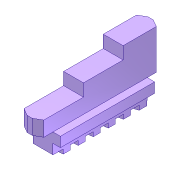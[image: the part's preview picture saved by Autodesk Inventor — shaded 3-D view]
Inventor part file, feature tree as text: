
AUTODESK INVENTOR PART (.ipt)
format: ipt  version: unknown  size: 337,408 bytes
history: native  units: in
note: dims shown in document units (in); Inventor stores cm internally (conversion verified against a paired STEP export)
features: extrude x7, sketch x7, fillet x1, projected_geometry x1
ambient origin geometry x8: Origin, YZ Plane, XZ Plane, XY Plane, X Axis, Y Axis, Z Axis, Center Point
feature tree (16):
  extrude  "Extrusion8"  Depth=0.1378in
  extrude  "Extrusion9"  Depth=0.0787in
  extrude  "Extrusion10"  Depth=0.315in
  extrude  "Extrusion11"  TaperAngle=30.0deg  [1 undecoded]
  extrude  "Extrusion13"  Depth=0.7874in TaperAngle=0.0deg
  extrude  "Extrusion14"  Depth=0.1969in TaperAngle=0.0deg
  fillet  "Fillet1"  Radius=0.315in
  extrude  "Extrusion16"  Depth=0.1181in
  sketch  "Sketch10"  dims[d51=0.0787in d52=0.1378in]
  sketch  "Sketch11"  dims[d53=0.0787in d54=0.0787in]
  sketch  "Sketch12"  dims[d55=0.0787in d56=0.315in]
  sketch  "Sketch13"  dims[d57=0.9843in d58=0.0in d59=30.0deg]
  sketch  "Sketch15"  dims[d60=30.0deg d61=0.7874in d62=0.0in]
  sketch  "Sketch16"  dims[d63=0.315in d64=0.1969in d65=0.0in d66=0.315in]
  sketch  "Sketch18"  dims[d67=0.0984in d68=0.0in d72=0.1181in d73=0.1181in d74=0.0787in d75=0.0in d76=0.2874in d79=0.0551in d81=0.0551in d83=0.0551in d85=0.0551in d87=0.0551in d89=0.0551in d90=0.0354in d91=0.0in d92=0.1181in d93=0.1181in d94=0.1181in d95=0.1181in d96=0.1181in d102=0.0008in d103=0.0118in d104=0.0118in d105=0.3937in d106=0.0in]
  projected_geometry  "Projected Loop1"
note: 1 required parameter value undecoded (feature->parameter linkage not recoverable at this tier; creation-order binding heuristic only, values carry confidence <= 0.55)
